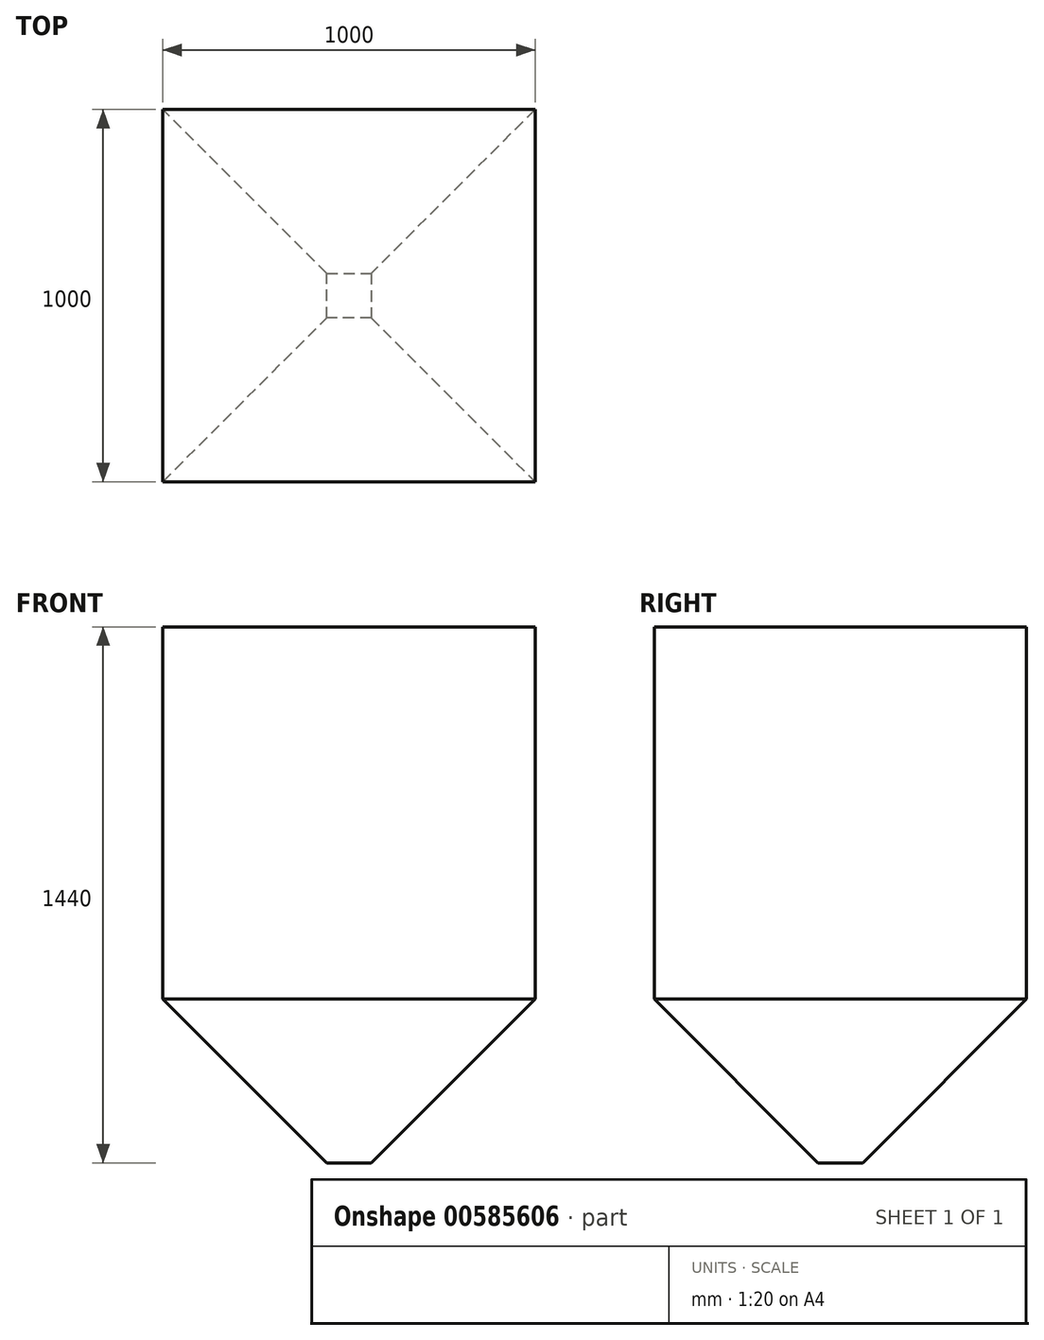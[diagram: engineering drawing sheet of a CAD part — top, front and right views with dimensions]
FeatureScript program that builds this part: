
annotation { "Feature Type Name" : "Feature", "Feature Type Description" : "" }
export const myFeature = defineFeature(function(context is Context, id is Id, definition is map)
    precondition{}
    {
        {
            var Q0;
            Q0=qCreatedBy(makeId("Top.planeOp"),FACE);
            var sketch = newSketch(context, id + "F0", { "sketchPlane" : qUnion([Q0])});
            skLineSegment(sketch, "E0.bottom", {"start": v(500, -500) * mm, "end": v(-500, -500) * mm});
            skLineSegment(sketch, "E0.top", {"start": v(500, 500) * mm, "end": v(-500, 500) * mm});
            skLineSegment(sketch, "E0.left", {"start": v(500, -500) * mm, "end": v(500, 500) * mm});
            skLineSegment(sketch, "E0.right", {"start": v(-500, -500) * mm, "end": v(-500, 500) * mm});
            skPoint(sketch, "E0.middle", {"position": v(0, 0) * mm});
            skSolve(sketch);
        }
        {
            var Q0;
            Q0 = qSketchRegion(id + "F0", true);
            extrude(context, id + "F1", {"entities" : qUnion([Q0]), "depth" : 1000 * mm, "offsetDistance" : 25 * mm, "hasSecondDirection" : true, "secondDirectionOppositeDirection" : true, "secondDirectionDepth" : 440 * mm, "hasSecondDirectionDraft" : true, "secondDirectionDraftAngle" : 45 * degree, "secondDirectionDraftPullDirection" : true});
        }
    });
